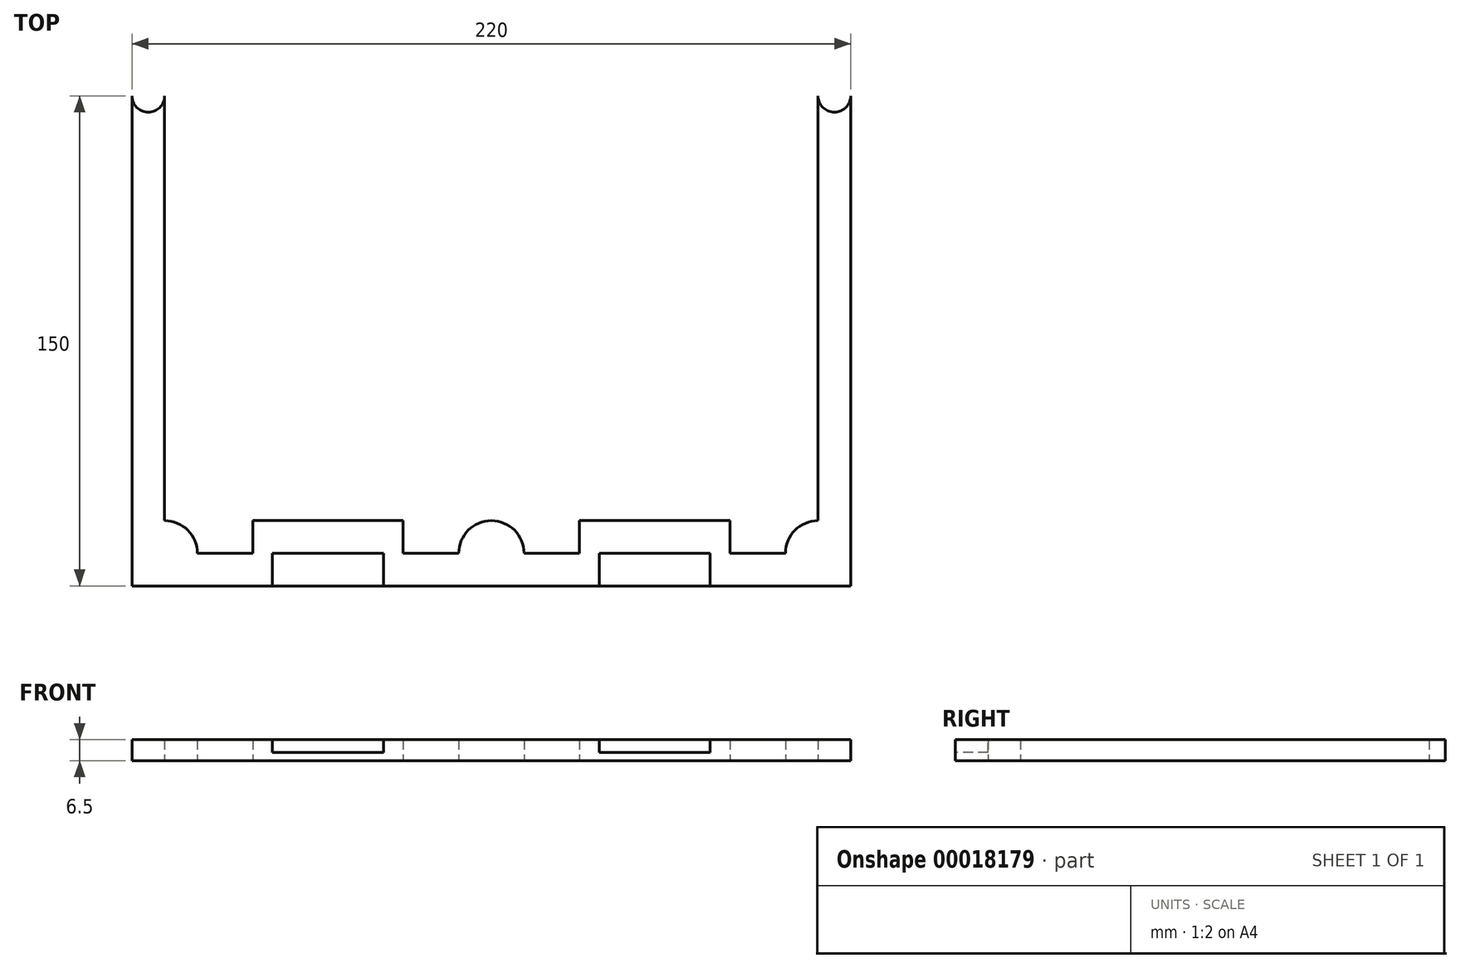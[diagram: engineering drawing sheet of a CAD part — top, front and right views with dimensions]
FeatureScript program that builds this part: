
annotation { "Feature Type Name" : "Feature", "Feature Type Description" : "" }
export const myFeature = defineFeature(function(context is Context, id is Id, definition is map)
    precondition{}
    {
        {
            var Q0;
            Q0=qCreatedBy(makeId("Top.planeOp"),FACE);
            var sketch = newSketch(context, id + "F0", { "sketchPlane" : qUnion([Q0])});
            skLineSegment(sketch, "E0.rect.bottom", {"start": v(110, -112.75) * mm, "end": v(110, -112.75) * mm});
            skLineSegment(sketch, "E0.rect.left", {"start": v(110, -112.75) * mm, "end": v(110, 37.25) * mm});
            skLineSegment(sketch, "E0.rect.right", {"start": v(-110, -112.75) * mm, "end": v(-110, 37.25) * mm});
            skPoint(sketch, "E0.rect.middle", {"position": v(0, 0) * mm});
            skLineSegment(sketch, "E1.rect.bottom", {"start": v(-100, -102.75) * mm, "end": v(-100, -102.75) * mm});
            skLineSegment(sketch, "E1.rect.left", {"start": v(-100, -92.75) * mm, "end": v(-100, 37.25) * mm});
            skLineSegment(sketch, "E1.rect.right", {"start": v(100, -92.75) * mm, "end": v(100, 37.25) * mm});
            skArc(sketch, "E2", {"start": v(-90, -102.75) * mm, "mid": v(-92.93, -95.68) * mm, "end": v(-100, -92.75) * mm});
            skArc(sketch, "E3", {"start": v(100, -92.75) * mm, "mid": v(92.93, -95.68) * mm, "end": v(90, -102.75) * mm});
            skArc(sketch, "E4", {"start": v(10, -102.75) * mm, "mid": v(0, -92.75) * mm, "end": v(-10, -102.75) * mm});
            skLineSegment(sketch, "E5", {"start": v(0, -112.75) * mm, "end": v(0, 112.75) * mm, "construction": true});
            skLineSegment(sketch, "E6", {"start": v(125.9, -112.75) * mm, "end": v(125.9, 37.25) * mm, "construction": true});
            skLineSegment(sketch, "E7", {"start": v(125.9, 37.25) * mm, "end": v(110, 37.25) * mm, "construction": true});
            skLineSegment(sketch, "E8", {"start": v(110, 37.25) * mm, "end": v(100, 37.25) * mm, "construction": true});
            skArc(sketch, "E9", {"start": v(100, 37.25) * mm, "mid": v(105, 32.25) * mm, "end": v(110, 37.25) * mm});
            skArc(sketch, "E10.MirrorCS", {"start": v(-100, 37.25) * mm, "mid": v(-105, 32.25) * mm, "end": v(-110, 37.25) * mm});
            skPoint(sketch, "E11.orphan", {"position": v(-100, 102.75) * mm});
            skPoint(sketch, "E12.orphan", {"position": v(-110, 112.75) * mm});
            skLineSegment(sketch, "E13", {"start": v(110, -112.75) * mm, "end": v(-110, -112.75) * mm});
            skLineSegment(sketch, "E14", {"start": v(100, -102.75) * mm, "end": v(100, -102.75) * mm});
            skLineSegment(sketch, "E15", {"start": v(10, -102.75) * mm, "end": v(90, -102.75) * mm});
            skLineSegment(sketch, "E16", {"start": v(-90, -102.75) * mm, "end": v(-10, -102.75) * mm});
            skLineSegment(sketch, "E17", {"start": v(50, -102.75) * mm, "end": v(50, 113.03) * mm, "construction": true});
            skLineSegment(sketch, "E18", {"start": v(73, -102.75) * mm, "end": v(73, -92.75) * mm});
            skLineSegment(sketch, "E19", {"start": v(73, -92.75) * mm, "end": v(50, -92.75) * mm});
            skLineSegment(sketch, "E20.MirrorCS", {"start": v(27, -92.75) * mm, "end": v(50, -92.75) * mm});
            skLineSegment(sketch, "E21.MirrorCS", {"start": v(27, -102.75) * mm, "end": v(27, -92.75) * mm});
            skLineSegment(sketch, "E22.MirrorCS", {"start": v(-27, -92.75) * mm, "end": v(-50, -92.75) * mm});
            skLineSegment(sketch, "E23.MirrorCS", {"start": v(-27, -102.75) * mm, "end": v(-27, -92.75) * mm});
            skLineSegment(sketch, "E24.MirrorCS", {"start": v(-73, -92.75) * mm, "end": v(-50, -92.75) * mm});
            skLineSegment(sketch, "E25.MirrorCS", {"start": v(-73, -102.75) * mm, "end": v(-73, -92.75) * mm});
            skSolve(sketch);
        }
        {
            var Q0;
            Q0 = qSketchRegion(id + "F0", true);
            extrude(context, id + "F1", {"entities" : qUnion([Q0]), "depth" : 6.5 * mm});
        }
        {
            var Q0;
            Q0=makeQuery(id+"F1.opExtrude","CAP_FACE",FACE,{"disambiguationData":[OSD([sQuery(id+"F0.wireOp",EDGE,"E0.rect.left"),sQuery(id+"F0.wireOp",EDGE,"E0.rect.right"),sQuery(id+"F0.wireOp",EDGE,"E1.rect.left"),sQuery(id+"F0.wireOp",EDGE,"E1.rect.right"),sQuery(id+"F0.wireOp",EDGE,"E2"),sQuery(id+"F0.wireOp",EDGE,"E3"),sQuery(id+"F0.wireOp",EDGE,"E4"),sQuery(id+"F0.wireOp",EDGE,"E9"),sQuery(id+"F0.wireOp",EDGE,"E10.MirrorCS"),sQuery(id+"F0.wireOp",EDGE,"E13"),sQuery(id+"F0.wireOp",EDGE,"E15"),sQuery(id+"F0.wireOp",EDGE,"E16"),sQuery(id+"F0.wireOp",EDGE,"E18"),sQuery(id+"F0.wireOp",EDGE,"E19"),sQuery(id+"F0.wireOp",EDGE,"E20.MirrorCS"),sQuery(id+"F0.wireOp",EDGE,"E21.MirrorCS"),sQuery(id+"F0.wireOp",EDGE,"E22.MirrorCS"),sQuery(id+"F0.wireOp",EDGE,"E23.MirrorCS"),sQuery(id+"F0.wireOp",EDGE,"E24.MirrorCS"),sQuery(id+"F0.wireOp",EDGE,"E25.MirrorCS")])],"isStart":false});
            var sketch = newSketch(context, id + "F2", { "sketchPlane" : qUnion([Q0])});
            skLineSegment(sketch, "E26", {"start": v(0, -112.75) * mm, "end": v(0, 0) * mm, "construction": true});
            skLineSegment(sketch, "E27", {"start": v(100, -102.75) * mm, "end": v(0, -102.75) * mm, "construction": true});
            skLineSegment(sketch, "E28", {"start": v(50, -102.75) * mm, "end": v(50, -112.75) * mm, "construction": true});
            skLineSegment(sketch, "E29", {"start": v(67, -102.75) * mm, "end": v(33, -102.75) * mm});
            skLineSegment(sketch, "E30", {"start": v(33, -102.75) * mm, "end": v(33, -112.75) * mm});
            skLineSegment(sketch, "E31", {"start": v(67, -102.75) * mm, "end": v(67, -112.75) * mm});
            skLineSegment(sketch, "E32", {"start": v(67, -112.75) * mm, "end": v(33, -112.75) * mm});
            skLineSegment(sketch, "E33.MirrorCS", {"start": v(-67, -102.75) * mm, "end": v(-33, -102.75) * mm});
            skLineSegment(sketch, "E34.MirrorCS", {"start": v(-33, -102.75) * mm, "end": v(-33, -112.75) * mm});
            skLineSegment(sketch, "E35.MirrorCS", {"start": v(-67, -102.75) * mm, "end": v(-67, -112.75) * mm});
            skLineSegment(sketch, "E36.MirrorCS", {"start": v(-67, -112.75) * mm, "end": v(-33, -112.75) * mm});
            skSolve(sketch);
        }
        {
            var Q0;
            Q0 = qSketchRegion(id + "F2", true);
            extrude(context, id + "F3", {"entities" : qUnion([Q0]), "operationType" : NewBodyOperationType.REMOVE, "oppositeDirection" : true, "depth" : 4 * mm});
        }
    });
